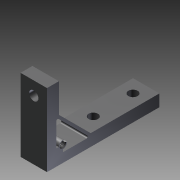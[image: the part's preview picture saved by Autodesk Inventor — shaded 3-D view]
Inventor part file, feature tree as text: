
AUTODESK INVENTOR PART (.ipt)
format: ipt  version: 2011 SP1 (Build 150282100, 282)  size: 166,912 bytes
history: native  units: mm
features: other x147, sketch x5, hole x3, extrude x1, revolve x1, thread x1
ambient origin geometry x8: Origin, YZ Plane, XZ Plane, XY Plane, X Axis, Y Axis, Z Axis, Center Point
bodies: Solid1 (feature_tree)
feature tree (158):
  extrude  "Extrusion1"  TaperAngle=360.0deg  [1 undecoded]
  revolve  "Revolution1"  [1 undecoded]
  thread  "Thread1"  [1 undecoded]
  hole  "Hole1"  [1 undecoded]
  hole  "Hole2"  [1 undecoded]
  hole  "Hole3"  [1 undecoded]
  other  "a10_to_bolt_XY"
  other  "a10_to_bolt_YZ"
  other  "a10_to_bolt_ZX"
  other  "a10_to_bolt_X"
  other  "a10_to_bolt_Y"
  other  "a10_to_bolt_Z"
  other  "a10_to_bolt_Center"
  other  "a11_to_bolt_XY"
  other  "a11_to_bolt_YZ"
  other  "a11_to_bolt_ZX"
  other  "a11_to_bolt_X"
  other  "a11_to_bolt_Y"
  other  "a11_to_bolt_Z"
  other  "a11_to_bolt_Center"
  other  "a13_to_bolt_XY"
  other  "a13_to_bolt_YZ"
  other  "a13_to_bolt_ZX"
  other  "a13_to_bolt_X"
  other  "a13_to_bolt_Y"
  other  "a13_to_bolt_Z"
  other  "a13_to_bolt_Center"
  other  "a14_to_bolt_XY"
  other  "a14_to_bolt_YZ"
  other  "a14_to_bolt_ZX"
  other  "a14_to_bolt_X"
  other  "a14_to_bolt_Y"
  other  "a14_to_bolt_Z"
  other  "a14_to_bolt_Center"
  other  "a15_to_bolt_XY"
  other  "a15_to_bolt_YZ"
  other  "a15_to_bolt_ZX"
  other  "a15_to_bolt_X"
  other  "a15_to_bolt_Y"
  other  "a15_to_bolt_Z"
  other  "a15_to_bolt_Center"
  other  "a16_to_bolt_XY"
  other  "a16_to_bolt_YZ"
  other  "a16_to_bolt_ZX"
  other  "a16_to_bolt_X"
  other  "a16_to_bolt_Y"
  other  "a16_to_bolt_Z"
  other  "a16_to_bolt_Center"
  other  "a17_to_bolt_XY"
  other  "a17_to_bolt_YZ"
  other  "a17_to_bolt_ZX"
  other  "a17_to_bolt_X"
  other  "a17_to_bolt_Y"
  other  "a17_to_bolt_Z"
  other  "a17_to_bolt_Center"
  other  "a18_XY"
  other  "a18_YZ"
  other  "a18_ZX"
  other  "a18_X"
  other  "a18_Y"
  other  "a18_Z"
  other  "a18_Center"
  other  "a19_to_bolt_XY"
  other  "a19_to_bolt_YZ"
  other  "a19_to_bolt_ZX"
  other  "a19_to_bolt_X"
  other  "a19_to_bolt_Y"
  other  "a19_to_bolt_Z"
  other  "a19_to_bolt_Center"
  other  "a1_to_bolt_XY"
  other  "a1_to_bolt_YZ"
  other  "a1_to_bolt_ZX"
  other  "a1_to_bolt_X"
  other  "a1_to_bolt_Y"
  other  "a1_to_bolt_Z"
  other  "a1_to_bolt_Center"
  other  "a20_to_bolt_XY"
  other  "a20_to_bolt_YZ"
  other  "a20_to_bolt_ZX"
  other  "a20_to_bolt_X"
  other  "a20_to_bolt_Y"
  other  "a20_to_bolt_Z"
  other  "a20_to_bolt_Center"
  other  "a2_to_bolt_XY"
  other  "a2_to_bolt_YZ"
  other  "a2_to_bolt_ZX"
  other  "a2_to_bolt_X"
  other  "a2_to_bolt_Y"
  other  "a2_to_bolt_Z"
  other  "a2_to_bolt_Center"
  other  "a3_to_bolt_XY"
  other  "a3_to_bolt_YZ"
  other  "a3_to_bolt_ZX"
  other  "a3_to_bolt_X"
  other  "a3_to_bolt_Y"
  other  "a3_to_bolt_Z"
  other  "a3_to_bolt_Center"
  other  "a4_to_bolt_XY"
  other  "a4_to_bolt_YZ"
  other  "a4_to_bolt_ZX"
  other  "a4_to_bolt_X"
  other  "a4_to_bolt_Y"
  other  "a4_to_bolt_Z"
  other  "a4_to_bolt_Center"
  other  "a5_to_bolt_XY"
  other  "a5_to_bolt_YZ"
  other  "a5_to_bolt_ZX"
  other  "a5_to_bolt_X"
  other  "a5_to_bolt_Y"
  other  "a5_to_bolt_Z"
  other  "a5_to_bolt_Center"
  other  "a6_to_bolt_XY"
  other  "a6_to_bolt_YZ"
  other  "a6_to_bolt_ZX"
  other  "a6_to_bolt_X"
  other  "a6_to_bolt_Y"
  other  "a6_to_bolt_Z"
  other  "a6_to_bolt_Center"
  other  "a7_to_bolt_XY"
  other  "a7_to_bolt_YZ"
  other  "a7_to_bolt_ZX"
  other  "a7_to_bolt_X"
  other  "a7_to_bolt_Y"
  other  "a7_to_bolt_Z"
  other  "a7_to_bolt_Center"
  other  "a8_to_bolt_XY"
  other  "a8_to_bolt_YZ"
  other  "a8_to_bolt_ZX"
  other  "a8_to_bolt_X"
  other  "a8_to_bolt_Y"
  other  "a8_to_bolt_Z"
  other  "a8_to_bolt_Center"
  other  "a9_to_bolt_XY"
  other  "a9_to_bolt_YZ"
  other  "a9_to_bolt_ZX"
  other  "a9_to_bolt_X"
  other  "a9_to_bolt_Y"
  other  "a9_to_bolt_Z"
  other  "a9_to_bolt_Center"
  other  "bracket_to_dummy_XY"
  other  "bracket_to_dummy_YZ"
  other  "bracket_to_dummy_ZX"
  other  "bracket_to_dummy_X"
  other  "bracket_to_dummy_Y"
  other  "bracket_to_dummy_Z"
  other  "bracket_to_dummy_Center"
  other  "h12_to_bolt_XY"
  other  "h12_to_bolt_YZ"
  other  "h12_to_bolt_ZX"
  other  "h12_to_bolt_X"
  other  "h12_to_bolt_Y"
  other  "h12_to_bolt_Z"
  other  "h12_to_bolt_Center"
  sketch  "Sketch_1"  dims[d0=20.0mm d1=0.0mm d2=360.0deg]
  sketch  "Sketch_10"  dims[d19=7.0mm d20=6.0mm d21=4.0mm d22=2.0mm d23=90.0deg d24=9.0mm d25=0.0mm d26=0.0mm d27=0.0mm d28=0.0mm d29=0.0mm d30=0.0mm d31=0.0mm d32=0.0mm]
  sketch  "Sketch3"  dims[d3=19.134mm d4=0.0mm]
  sketch  "Sketch4"  dims[d5=7.0mm d6=6.0mm d7=4.0mm d8=2.0mm d9=90.0deg d10=9.0mm d11=0.0mm]
  sketch  "Sketch5"  dims[d12=7.0mm d13=6.0mm d14=4.0mm d15=2.0mm d16=90.0deg d17=9.0mm d18=0.0mm]
note: 6 required parameter values undecoded (feature->parameter linkage not recoverable at this tier; creation-order binding heuristic only, values carry confidence <= 0.55)
